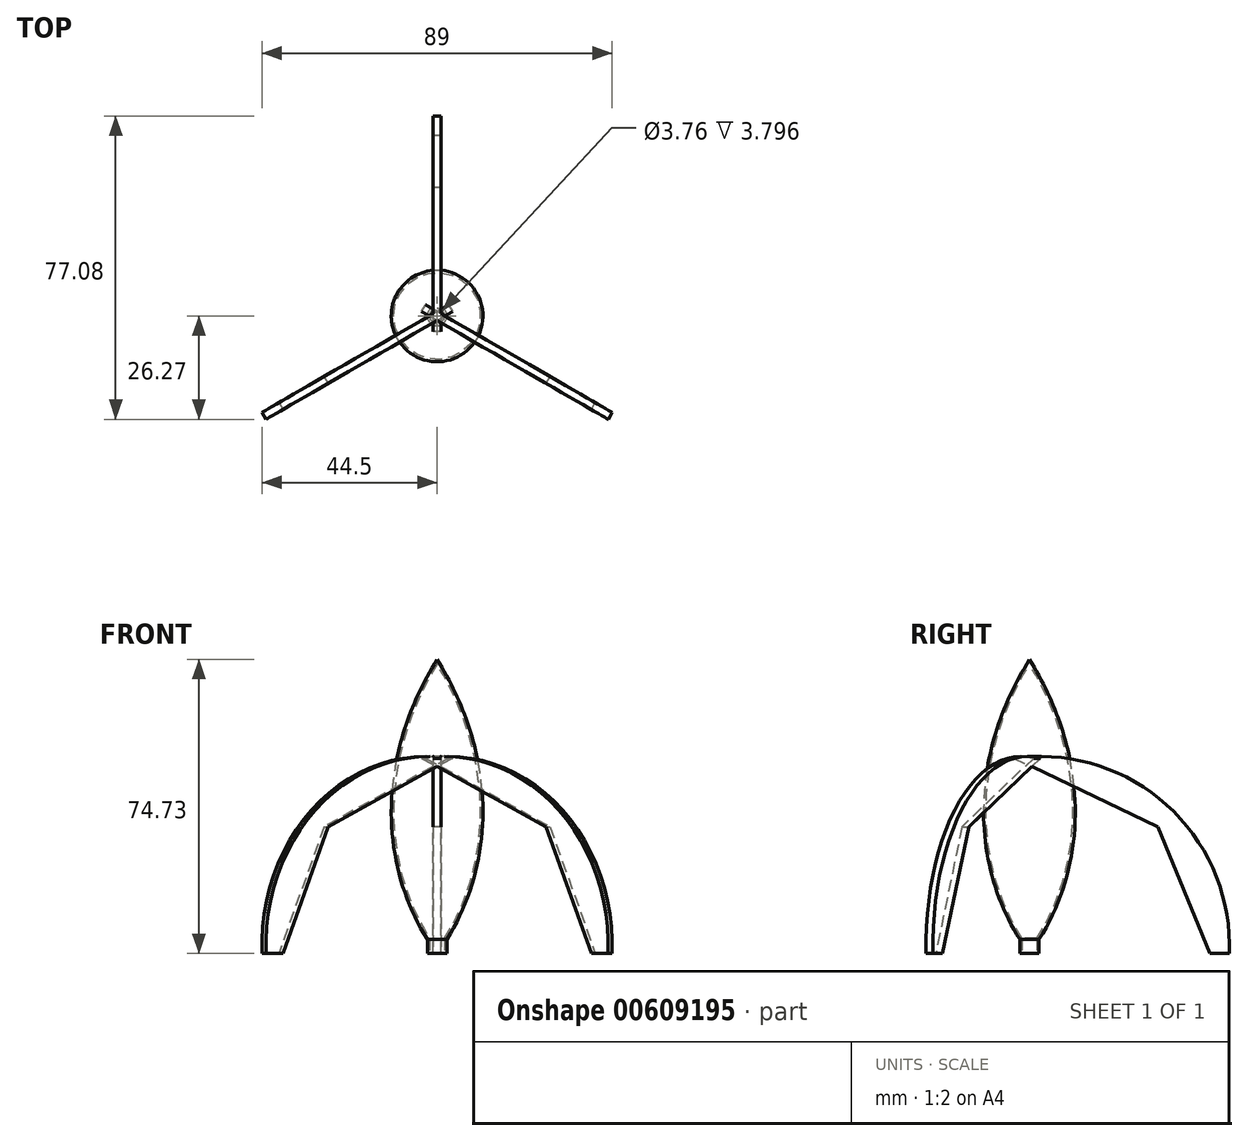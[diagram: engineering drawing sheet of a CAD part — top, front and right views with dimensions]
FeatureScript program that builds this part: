
annotation { "Feature Type Name" : "Feature", "Feature Type Description" : "" }
export const myFeature = defineFeature(function(context is Context, id is Id, definition is map)
    precondition{}
    {
        {
            var Q0;
            Q0=qCreatedBy(makeId("Front.planeOp"),FACE);
            var sketch = newSketch(context, id + "F0", { "sketchPlane" : qUnion([Q0])});
            skLineSegment(sketch, "E0", {"start": v(0, 0) * mm, "end": v(0, 74.73) * mm});
            skFitSpline(sketch, "E1", {"points": [v(0, 74.73) * mm, v(0, 0) * mm, v(71.47, -38.82) * mm], "startDerivative": vector(-103.65, -167.42) * mm, "endDerivative": vector(175.72, -56.46) * mm});
            skSolve(sketch);
        }
        {
            var Q0;
            Q0=makeQuery(id+"F0.imprint","IMPRINT",FACE,{"disambiguationData":[TD([[makeQuery(id+"F0.imprint","IMPRINT",EDGE,{"derivedFrom":sQuery(id+"F0.wireOp",EDGE,"E0")}),1.0]])]});
            var Q1;
            Q1=sQuery(id+"F0.wireOp",EDGE,"E0");
            revolve(context, id + "F1", {"surfaceOperationType" : NewSurfaceOperationType.NEW, "entities" : qUnion([Q0]), "axis" : qUnion([Q1]), "revolveType" : RevolveType.FULL});
        }
        {
            var Q0;
            Q0=qCreatedBy(makeId("Top.planeOp"),FACE);
            var sketch = newSketch(context, id + "F2", { "sketchPlane" : qUnion([Q0])});
            skCircle(sketch, "E2", {"center": v(-50.88, 0) * mm, "radius": 5.56 * mm});
            skCircle(sketch, "E3", {"center": v(0, 0) * mm, "radius": 13 * mm});
            skCircle(sketch, "E4.0", {"center": v(0, 0) * mm, "radius": 9 * mm});
            skSolve(sketch);
        }
        {
            var Q0;
            Q0=qCreatedBy(makeId("Top.planeOp"),FACE);
            var sketch = newSketch(context, id + "F3", { "sketchPlane" : qUnion([Q0])});
            skCircle(sketch, "E5", {"center": v(0, 0) * mm, "radius": 2.48 * mm});
            skSolve(sketch);
        }
        {
            var Q0;
            Q0 = qSketchRegion(id + "F3", true);
            extrude(context, id + "F4", {"entities" : qUnion([Q0]), "operationType" : NewBodyOperationType.ADD, "depth" : 6 * mm, "offsetDistance" : 25 * mm});
        }
        {
            var Q0;
            Q0=qCreatedBy(makeId("Right.planeOp"),FACE);
            var sketch = newSketch(context, id + "F5", { "sketchPlane" : qUnion([Q0])});
            skLineSegment(sketch, "E6", {"start": v(45.82, 0) * mm, "end": v(50.77, 0) * mm});
            skArc(sketch, "E7", {"start": v(50.77, 0) * mm, "mid": v(35.04, 37.6) * mm, "end": v(-3.92, 49.64) * mm});
            skLineSegment(sketch, "E8", {"start": v(-3.92, 49.64) * mm, "end": v(32.58, 32.24) * mm});
            skLineSegment(sketch, "E9", {"start": v(32.58, 32.24) * mm, "end": v(45.82, 0) * mm});
            skSolve(sketch);
        }
        {
            var Q0;
            Q0=makeQuery(id+"F5.imprint","IMPRINT",FACE,{"disambiguationData":[TD([[makeQuery(id+"F5.imprint","IMPRINT",EDGE,{"derivedFrom":sQuery(id+"F5.wireOp",EDGE,"E6")}),1.0]])]});
            extrude(context, id + "F6", {"entities" : qUnion([Q0]), "endBound" : BoundingType.SYMMETRIC, "depth" : 2 * mm, "offsetDistance" : 25 * mm});
        }
        {
            var Q0;
            Q0=makeQuery(id+"F6.opExtrude","SWEPT_BODY",BODY,{"disambiguationData":[OSD([sQuery(id+"F5.wireOp",EDGE,"E6"),sQuery(id+"F5.wireOp",EDGE,"E7"),sQuery(id+"F5.wireOp",EDGE,"E8"),sQuery(id+"F5.wireOp",EDGE,"E9")])]});
            var Q1;
            Q1=makeQuery(id+"FjEwfB2FWlr5mb4_1.boolean.opBoolean","SPLIT",FACE,{"disambiguationData":[TD([makeQuery(id+"FjEwfB2FWlr5mb4_1.opExtrude","CAP_FACE",FACE,{"disambiguationData":[OSD([sQuery(id+"F2.wireOp",EDGE,"E3"),sQuery(id+"F2.wireOp",EDGE,"E4.0")])],"isStart":false})])],"derivedFrom":makeQuery(id+"F1.opRevolve","SWEPT_FACE",FACE,{"disambiguationData":[OSD([sQuery(id+"F0.wireOp",EDGE,"E1")])]})});
            circularPattern(context, id + "F7", {"entities" : qUnion([Q0]), "axis" : qUnion([Q1]), "angle" : 360 * degree, "instanceCount" : 3, "equalSpace" : true});
        }
        {
            var Q0;
            Q0=makeQuery(id+"F4.opExtrude","CAP_FACE",FACE,{"disambiguationData":[OSD([sQuery(id+"F3.wireOp",EDGE,"E5")])],"isStart":true});
            shell(context, id + "F8", {"entities" : qUnion([Q0]), "thickness" : 0.6 * mm});
        }
    });
